# Revit family: Haworth_Janus_Quinta_Table_Cocktail
name_source: partatom
category: Furniture
revit_build: Autodesk Revit 2018 (Build: 20170223_1515(x64)
units: mm (PartAtom-declared; Revit-internal decimal feet)

## family parameters
Always vertical = Yes
Cut with Voids When Loaded = No
OmniClass Number = 23.40.70.14.64.21
OmniClass Title = Systems Furniture
Room Calculation Point = No
Shared = No
Work Plane-Based = No

## types (2) — shared parameters
Actual Width = 43 1/4"
Assembly Code = E2020200
Glide Finish = Haworth _ Polymer _ Black
Manufacturer = Haworth
Revision Number = 2
Size = Verify Final Dim. w/ Haworth
URL = http://www.haworth.com
URL - Product = https://www.haworth.com
Warranty = https://www.haworth.com

## per-type parameters (varying)
| type | Actual Depth | Actual Height | Description | Large | Leg Height | Model | Small | Top Thickness |
| HCJC-QN-TOR43-W - Small | 23 3/4" | 10 1/4" | Haworth Janus Quinta - Small Cocktail Table | No | 10 1/4" | HCJC-QN-TOR43-W | Yes | 1 187/256" |
| HCJC-QN-TOR43-J - Large | 25 1/2" | 17" | Haworth Janus Quinta - Large Cocktail Table | Yes | 15 35/256" | HCJC-QN-TOR43-J | No | 1 221/256" |

## geometry (parser evidence)
native form markers: Sweep x2
no freeform markers — native parametric forms only
